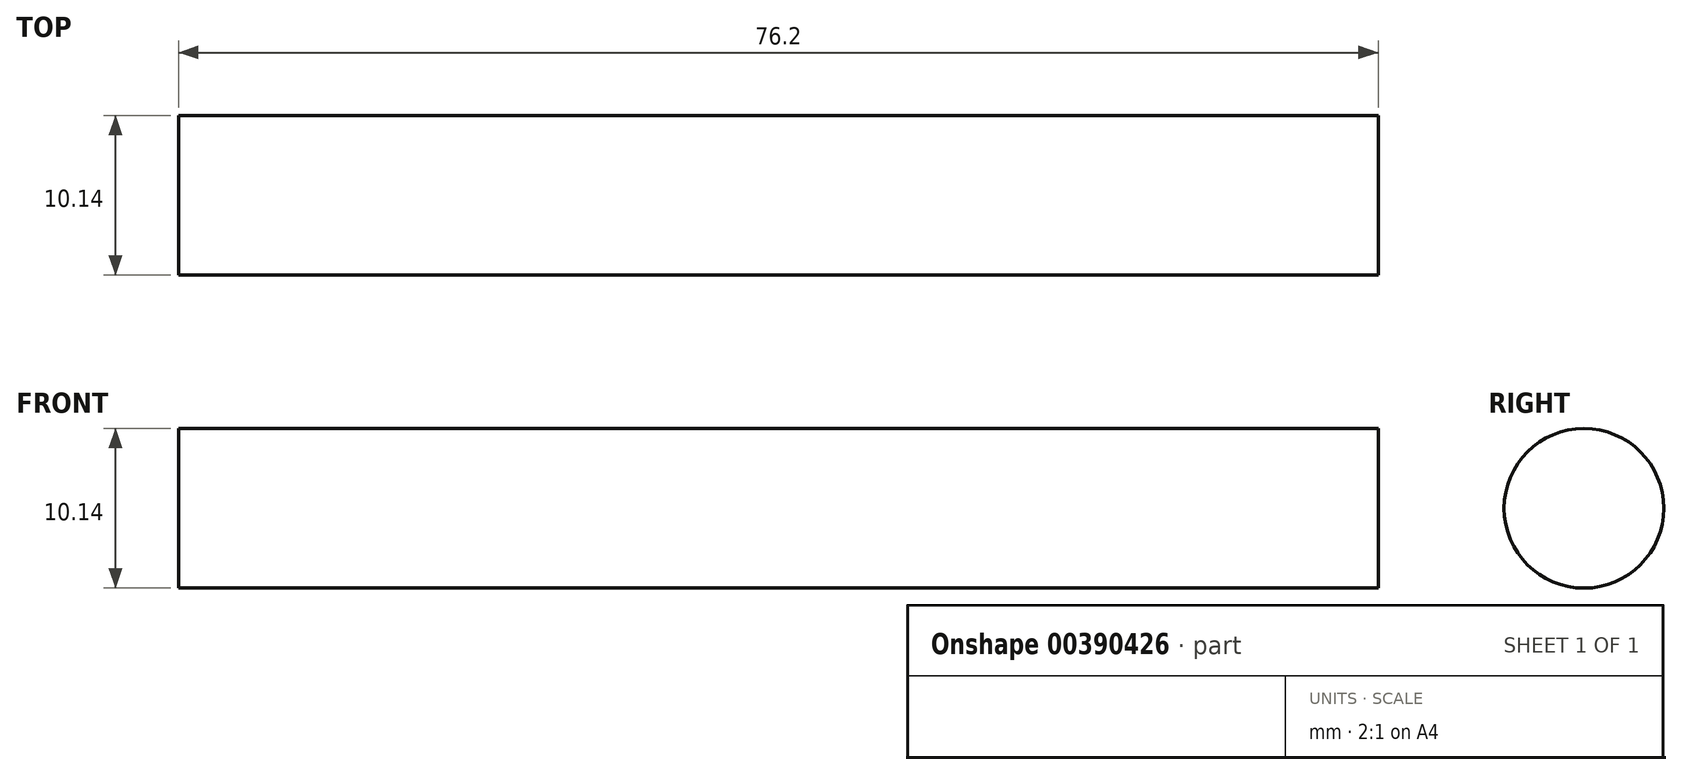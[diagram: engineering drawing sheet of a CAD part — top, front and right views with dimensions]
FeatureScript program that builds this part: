
annotation { "Feature Type Name" : "Feature", "Feature Type Description" : "" }
export const myFeature = defineFeature(function(context is Context, id is Id, definition is map)
    precondition{}
    {
        {
            var Q0;
            Q0=qCreatedBy(makeId("Right.planeOp"),FACE);
            var sketch = newSketch(context, id + "F0", { "sketchPlane" : qUnion([Q0])});
            skCircle(sketch, "E0", {"center": v(0, 0) * mm, "radius": 5.07 * mm});
            skSolve(sketch);
        }
        {
            var Q0;
            Q0=makeQuery(id+"F0.imprint","IMPRINT",FACE,{"disambiguationData":[TD([[makeQuery(id+"F0.imprint","IMPRINT",EDGE,{"derivedFrom":sQuery(id+"F0.wireOp",EDGE,"E0")}),1.0]])]});
            extrude(context, id + "F1", {"entities" : qUnion([Q0]), "depth" : 76.2 * mm});
        }
    });
